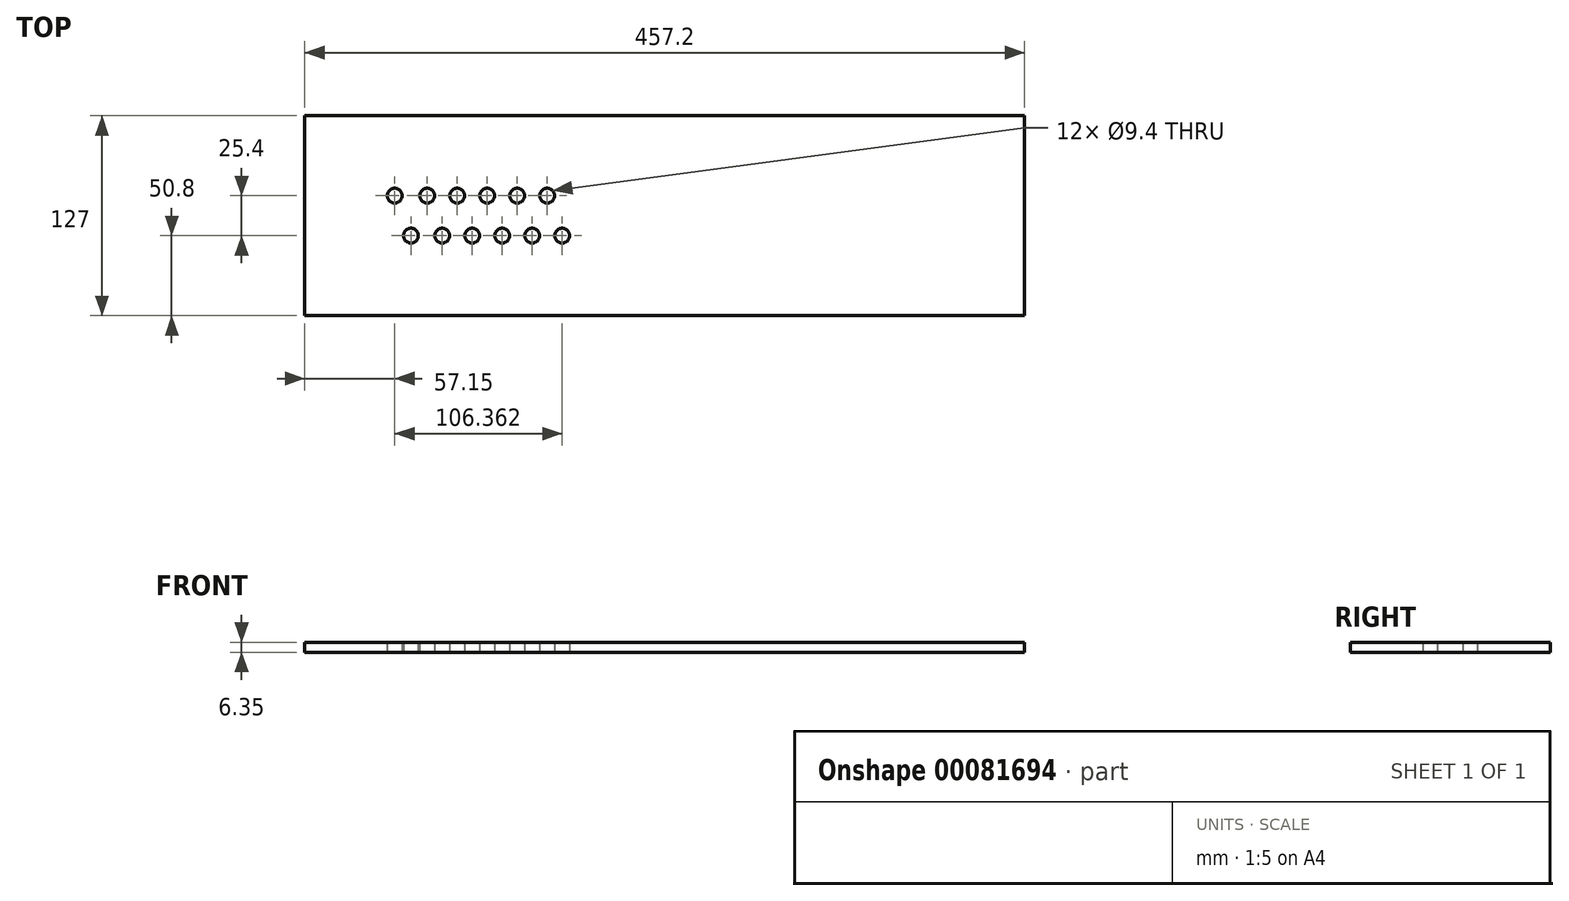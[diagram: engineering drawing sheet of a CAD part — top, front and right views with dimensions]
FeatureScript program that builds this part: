
annotation { "Feature Type Name" : "Feature", "Feature Type Description" : "" }
export const myFeature = defineFeature(function(context is Context, id is Id, definition is map)
    precondition{}
    {
        {
            var Q0;
            Q0=qCreatedBy(makeId("Top.planeOp"),FACE);
            var sketch = newSketch(context, id + "F0", { "sketchPlane" : qUnion([Q0])});
            skLineSegment(sketch, "E0.bottom", {"start": v(0, 0) * mm, "end": v(457.2, 0) * mm});
            skLineSegment(sketch, "E0.top", {"start": v(0, 127) * mm, "end": v(457.2, 127) * mm});
            skLineSegment(sketch, "E0.left", {"start": v(0, 0) * mm, "end": v(0, 127) * mm});
            skLineSegment(sketch, "E0.right", {"start": v(457.2, 0) * mm, "end": v(457.2, 127) * mm});
            skLineSegment(sketch, "E1", {"start": v(57.15, 127) * mm, "end": v(57.15, 0) * mm, "construction": true});
            skLineSegment(sketch, "E2", {"start": v(67.47, 127) * mm, "end": v(67.47, 0) * mm, "construction": true});
            skLineSegment(sketch, "E3", {"start": v(77.79, 127) * mm, "end": v(77.79, 0) * mm, "construction": true});
            skLineSegment(sketch, "E4", {"start": v(87.31, 127) * mm, "end": v(87.31, 0) * mm, "construction": true});
            skLineSegment(sketch, "E5", {"start": v(106.36, 127) * mm, "end": v(106.36, 0) * mm, "construction": true});
            skLineSegment(sketch, "E6", {"start": v(115.89, 127) * mm, "end": v(115.89, 0) * mm, "construction": true});
            skLineSegment(sketch, "E7", {"start": v(125.41, 127) * mm, "end": v(125.41, 0) * mm, "construction": true});
            skLineSegment(sketch, "E8", {"start": v(96.84, 127) * mm, "end": v(96.84, 0) * mm, "construction": true});
            skLineSegment(sketch, "E9", {"start": v(134.94, 127) * mm, "end": v(134.94, 0) * mm, "construction": true});
            skLineSegment(sketch, "E10", {"start": v(144.46, 127) * mm, "end": v(144.46, 0) * mm, "construction": true});
            skLineSegment(sketch, "E11", {"start": v(153.99, 127) * mm, "end": v(153.99, 0) * mm, "construction": true});
            skLineSegment(sketch, "E12", {"start": v(163.51, 127) * mm, "end": v(163.51, 0) * mm, "construction": true});
            skLineSegment(sketch, "E13", {"start": v(57.15, 63.5) * mm, "end": v(163.51, 63.5) * mm, "construction": true});
            skLineSegment(sketch, "E14", {"start": v(57.15, 76.2) * mm, "end": v(163.51, 76.2) * mm, "construction": true});
            skLineSegment(sketch, "E15", {"start": v(57.15, 50.8) * mm, "end": v(163.51, 50.8) * mm, "construction": true});
            skCircle(sketch, "E16", {"center": v(57.15, 76.2) * mm, "radius": 4.7 * mm});
            skCircle(sketch, "E17", {"center": v(67.47, 50.8) * mm, "radius": 4.7 * mm});
            skCircle(sketch, "E18", {"center": v(77.79, 76.2) * mm, "radius": 4.7 * mm});
            skCircle(sketch, "E19", {"center": v(87.31, 50.8) * mm, "radius": 4.7 * mm});
            skCircle(sketch, "E20", {"center": v(96.84, 76.2) * mm, "radius": 4.7 * mm});
            skCircle(sketch, "E21", {"center": v(106.36, 50.8) * mm, "radius": 4.7 * mm});
            skCircle(sketch, "E22", {"center": v(115.89, 76.2) * mm, "radius": 4.7 * mm});
            skCircle(sketch, "E23", {"center": v(125.41, 50.8) * mm, "radius": 4.7 * mm});
            skCircle(sketch, "E24", {"center": v(134.94, 76.2) * mm, "radius": 4.7 * mm});
            skCircle(sketch, "E25", {"center": v(144.46, 50.8) * mm, "radius": 4.7 * mm});
            skCircle(sketch, "E26", {"center": v(153.99, 76.2) * mm, "radius": 4.7 * mm});
            skCircle(sketch, "E27", {"center": v(163.51, 50.8) * mm, "radius": 4.7 * mm});
            skSolve(sketch);
        }
        {
            var Q0;
            Q0=makeQuery(id+"F0.imprint","IMPRINT",FACE,{"disambiguationData":[TD([[makeQuery(id+"F0.imprint","IMPRINT",EDGE,{"derivedFrom":sQuery(id+"F0.wireOp",EDGE,"E0.bottom")}),1.0]])]});
            extrude(context, id + "F1", {"entities" : qUnion([Q0]), "depth" : 6.35 * mm});
        }
    });
